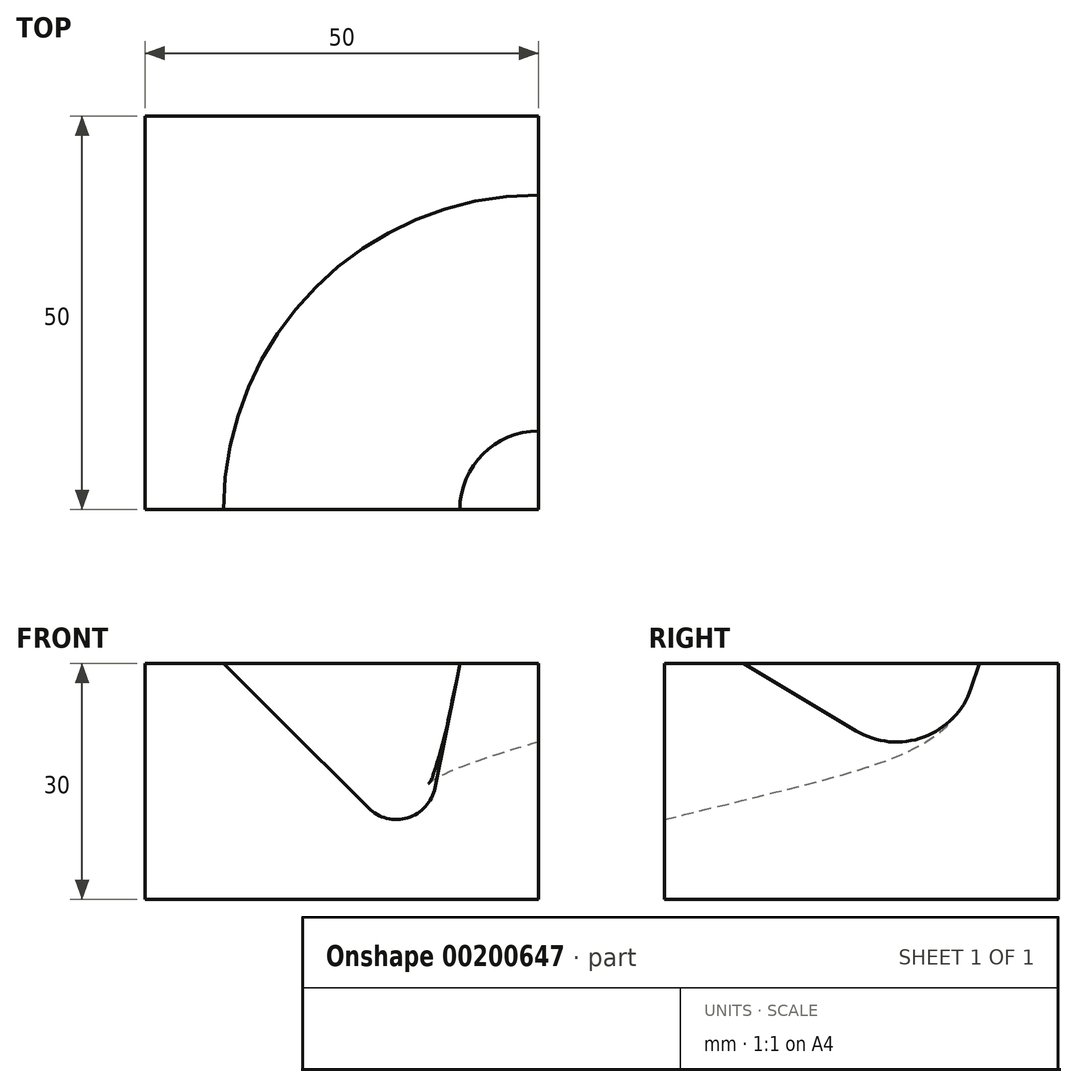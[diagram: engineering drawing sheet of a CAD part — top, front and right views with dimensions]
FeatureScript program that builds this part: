
annotation { "Feature Type Name" : "Feature", "Feature Type Description" : "" }
export const myFeature = defineFeature(function(context is Context, id is Id, definition is map)
    precondition{}
    {
        {
            var Q0;
            Q0=qCreatedBy(makeId("Top.planeOp"),FACE);
            var sketch = newSketch(context, id + "F0", { "sketchPlane" : qUnion([Q0])});
            skLineSegment(sketch, "E0.bottom", {"start": v(0, 0) * mm, "end": v(-50, 0) * mm});
            skLineSegment(sketch, "E0.top", {"start": v(0, 50) * mm, "end": v(-50, 50) * mm});
            skLineSegment(sketch, "E0.left", {"start": v(0, 0) * mm, "end": v(0, 50) * mm});
            skLineSegment(sketch, "E0.right", {"start": v(-50, 0) * mm, "end": v(-50, 50) * mm});
            skSolve(sketch);
        }
        {
            var Q0;
            Q0=makeQuery(id+"F0.imprint","IMPRINT",FACE,{"disambiguationData":[TD([[makeQuery(id+"F0.imprint","IMPRINT",EDGE,{"derivedFrom":sQuery(id+"F0.wireOp",EDGE,"E0.bottom")}),-1.0]])]});
            extrude(context, id + "F1", {"entities" : qUnion([Q0]), "depth" : 30 * mm});
        }
        {
            var Q0;
            Q0=makeQuery(id+"F1.opExtrude","CAP_FACE",FACE,{"disambiguationData":[OSD([sQuery(id+"F0.wireOp",EDGE,"E0.bottom"),sQuery(id+"F0.wireOp",EDGE,"E0.top"),sQuery(id+"F0.wireOp",EDGE,"E0.left"),sQuery(id+"F0.wireOp",EDGE,"E0.right")])],"isStart":false});
            var sketch = newSketch(context, id + "F2", { "sketchPlane" : qUnion([Q0])});
            skArc(sketch, "E1", {"start": v(-10, 0) * mm, "mid": v(-7.07, 7.07) * mm, "end": v(0, 10) * mm});
            skArc(sketch, "E2", {"start": v(-40, 0) * mm, "mid": v(-28.28, 28.28) * mm, "end": v(0, 40) * mm});
            skSolve(sketch);
        }
        {
            var Q0;
            Q0=makeQuery(id+"F1.opExtrude","SWEPT_FACE",FACE,{"disambiguationData":[OSD([sQuery(id+"F0.wireOp",EDGE,"E0.bottom")])]});
            var sketch = newSketch(context, id + "F3", { "sketchPlane" : qUnion([Q0])});
            skLineSegment(sketch, "E3", {"start": v(-40, 30) * mm, "end": v(-21.6, 11.6) * mm});
            skLineSegment(sketch, "E4", {"start": v(-13.17, 14.16) * mm, "end": v(-10, 30) * mm});
            skPoint(sketch, "E5.visualSharp", {"position": v(-15, 5) * mm});
            skArc(sketch, "E5.filletArc", {"start": v(-21.6, 11.6) * mm, "mid": v(-16.62, 10.36) * mm, "end": v(-13.17, 14.16) * mm});
            skSolve(sketch);
        }
        {
            var Q0;
            Q0=makeQuery(id+"F1.opExtrude","SWEPT_FACE",FACE,{"disambiguationData":[OSD([sQuery(id+"F0.wireOp",EDGE,"E0.left")])]});
            var sketch = newSketch(context, id + "F4", { "sketchPlane" : qUnion([Q0])});
            skLineSegment(sketch, "E6", {"start": v(10, 30) * mm, "end": v(24.31, 21.41) * mm});
            skLineSegment(sketch, "E7", {"start": v(38.94, 26.83) * mm, "end": v(40, 30) * mm});
            skPoint(sketch, "E8.visualSharp", {"position": v(35, 15) * mm});
            skArc(sketch, "E8.filletArc", {"start": v(24.31, 21.41) * mm, "mid": v(32.92, 20.6) * mm, "end": v(38.94, 26.83) * mm});
            skSolve(sketch);
        }
        {
            var Q1;
            {var subQ0=sQuery(id+"F3.wireOp",EDGE,"E3");Q1=makeQuery(id+"F3.imprint","IMPRINT",FACE,{"disambiguationData":[TD([[makeQuery(id+"F3.imprint","IMPRINT",EDGE,{"derivedFrom":subQ0}),1.0]])]});}
            var Q2;
            {var subQ0=sQuery(id+"F4.wireOp",EDGE,"E6");Q2=makeQuery(id+"F4.imprint","IMPRINT",FACE,{"disambiguationData":[TD([[makeQuery(id+"F4.imprint","IMPRINT",EDGE,{"derivedFrom":subQ0}),1.0]])]});}
            var Q3;
            Q3=sQuery(id+"F2.wireOp",EDGE,"E1");
            var Q4;
            Q4=sQuery(id+"F2.wireOp",EDGE,"E2");
            loft(context, id + "F5", {"addGuides" : true, "sheetProfilesArray" : [{ "sheetProfileEntities" : qUnion([Q1]) }, { "sheetProfileEntities" : qUnion([Q2]) }], "guidesArray" : [{ "guideEntities" : qUnion([Q3]), "guideDerivativeType" : LoftGuideDerivativeType.DEFAULT, "guideDerivativeMagnitude" : 1 }, { "guideEntities" : qUnion([Q4]), "guideDerivativeType" : LoftGuideDerivativeType.DEFAULT, "guideDerivativeMagnitude" : 1 }]});
        }
        {
            var Q0;
            {var subQ0=sQuery(id+"F4.wireOp",EDGE,"E6");var subQ3=sQuery(id+"F3.wireOp",EDGE,"E3");Q0=makeQuery(id+"F5.opLoft","SWEPT_BODY",BODY,{"disambiguationData":[OSD([sQuery(id+"F2.wireOp",EDGE,"E1"),sQuery(id+"F2.wireOp",EDGE,"E2"),makeQuery(id+"F3.imprint","IMPRINT",FACE,{"disambiguationData":[TD([[makeQuery(id+"F3.imprint","IMPRINT",EDGE,{"derivedFrom":subQ3}),1.0]])]}),makeQuery(id+"F4.imprint","IMPRINT",FACE,{"disambiguationData":[TD([[makeQuery(id+"F4.imprint","IMPRINT",EDGE,{"derivedFrom":subQ0}),1.0]])]})])]});}
            var Q1;
            Q1=makeQuery(id+"F1.opExtrude","SWEPT_BODY",BODY,{"disambiguationData":[OSD([sQuery(id+"F0.wireOp",EDGE,"E0.bottom"),sQuery(id+"F0.wireOp",EDGE,"E0.top"),sQuery(id+"F0.wireOp",EDGE,"E0.left"),sQuery(id+"F0.wireOp",EDGE,"E0.right")])]});
            booleanBodies(context, id + "F6", {"operationType" : BooleanOperationType.SUBTRACTION, "tools" : qUnion([Q0]), "targets" : qUnion([Q1])});
        }
    });
